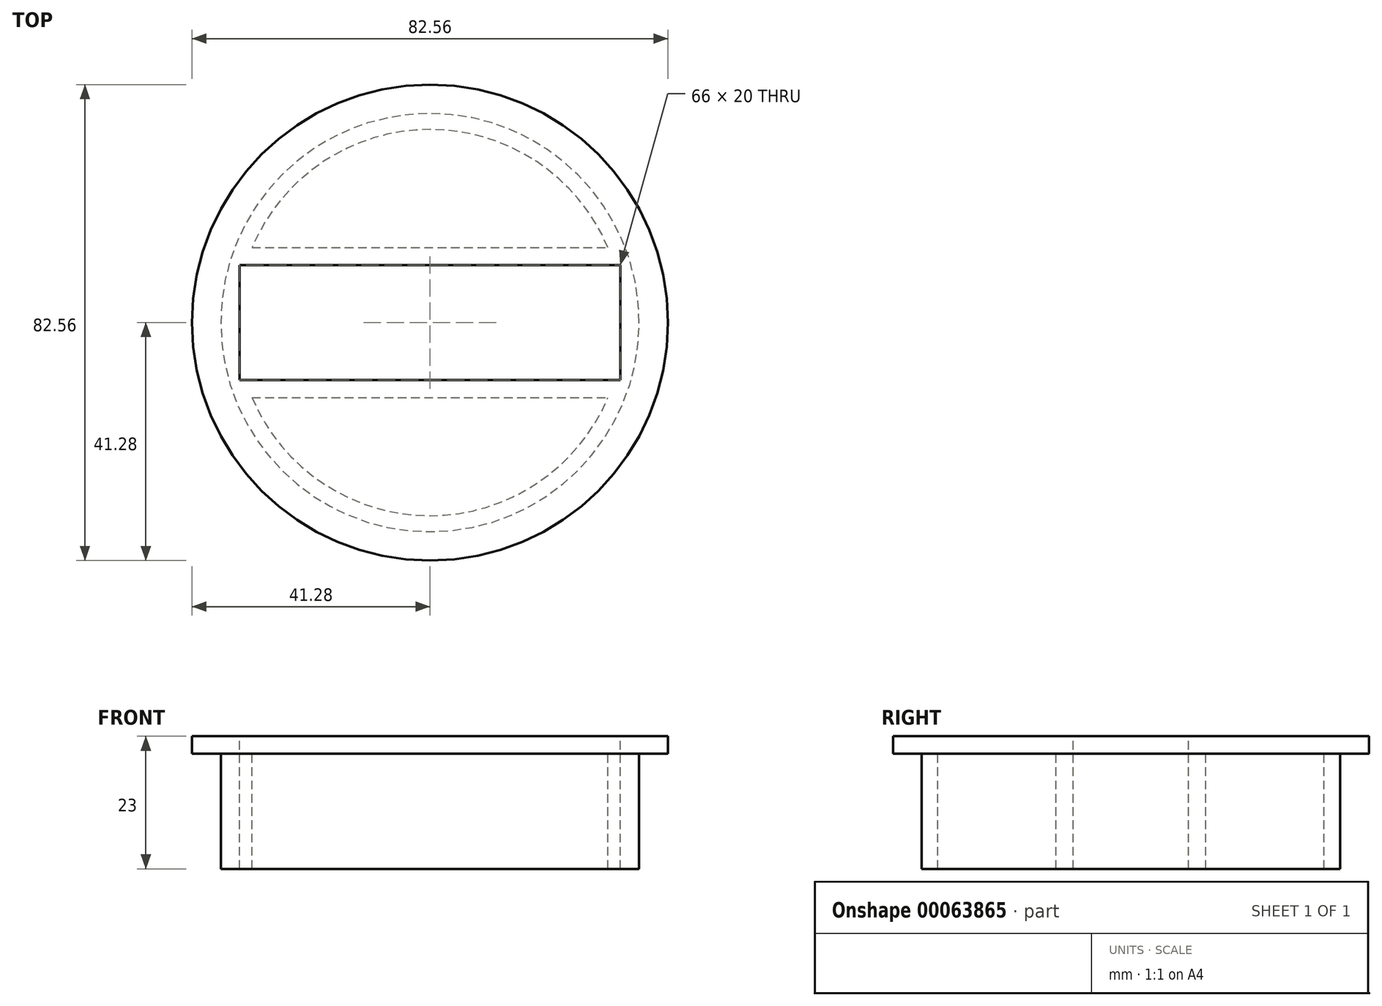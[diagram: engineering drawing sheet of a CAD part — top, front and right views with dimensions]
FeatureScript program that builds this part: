
annotation { "Feature Type Name" : "Feature", "Feature Type Description" : "" }
export const myFeature = defineFeature(function(context is Context, id is Id, definition is map)
    precondition{}
    {
        {
            var Q0;
            Q0=qCreatedBy(makeId("Top.planeOp"),FACE);
            var sketch = newSketch(context, id + "F0", { "sketchPlane" : qUnion([Q0])});
            skCircle(sketch, "E0", {"center": v(0, 0) * mm, "radius": 41.27 * mm});
            skSolve(sketch);
        }
        {
            var Q0;
            Q0 = qSketchRegion(id + "F0", true);
            extrude(context, id + "F1", {"entities" : qUnion([Q0]), "depth" : 3 * mm});
        }
        {
            var Q0;
            Q0=makeQuery(id+"F1.opExtrude","CAP_FACE",FACE,{"disambiguationData":[OSD([sQuery(id+"F0.wireOp",EDGE,"E0")])],"isStart":false});
            var sketch = newSketch(context, id + "F2", { "sketchPlane" : qUnion([Q0])});
            skLineSegment(sketch, "E1.rect.bottom", {"start": v(-33, -10) * mm, "end": v(33, -10) * mm});
            skLineSegment(sketch, "E1.rect.top", {"start": v(-33, 10) * mm, "end": v(33, 10) * mm});
            skLineSegment(sketch, "E1.rect.left", {"start": v(-33, -10) * mm, "end": v(-33, 10) * mm});
            skLineSegment(sketch, "E1.rect.right", {"start": v(33, -10) * mm, "end": v(33, 10) * mm});
            skPoint(sketch, "E1.rect.middle", {"position": v(0, 0) * mm});
            skSolve(sketch);
        }
        {
            var Q0;
            Q0=makeQuery(id+"F2.imprint","IMPRINT",FACE,{"disambiguationData":[TD([[makeQuery(id+"F2.imprint","IMPRINT",EDGE,{"derivedFrom":sQuery(id+"F2.wireOp",EDGE,"E1.rect.bottom")}),1.0]])]});
            extrude(context, id + "F3", {"entities" : qUnion([Q0]), "operationType" : NewBodyOperationType.REMOVE, "endBound" : BoundingType.THROUGH_ALL, "oppositeDirection" : true, "depth" : 25 * mm});
        }
        {
            var Q0;
            Q0=makeQuery(id+"F1.opExtrude","CAP_FACE",FACE,{"disambiguationData":[OSD([sQuery(id+"F0.wireOp",EDGE,"E0")])],"isStart":true});
            var sketch = newSketch(context, id + "F4", { "sketchPlane" : qUnion([Q0])});
            skCircle(sketch, "E2", {"center": v(0, 0) * mm, "radius": 36.5 * mm});
            skArc(sketch, "E3", {"start": v(30.87, 13) * mm, "mid": v(0, 33.5) * mm, "end": v(-30.87, 13) * mm});
            skLineSegment(sketch, "E4", {"start": v(33.5, 0) * mm, "end": v(36.5, 0) * mm});
            skLineSegment(sketch, "E5.0", {"start": v(-30.87, -13) * mm, "end": v(30.87, -13) * mm});
            skLineSegment(sketch, "E6.0", {"start": v(-30.87, 13) * mm, "end": v(30.87, 13) * mm});
            skCircle(sketch, "E7.0", {"center": v(0, 0) * mm, "radius": 36.27 * mm});
            skLineSegment(sketch, "E8.rect.bottom", {"start": v(-33, 10) * mm, "end": v(33, 10) * mm});
            skLineSegment(sketch, "E8.rect.top", {"start": v(-33, -10) * mm, "end": v(33, -10) * mm});
            skLineSegment(sketch, "E8.rect.left", {"start": v(-33, 10) * mm, "end": v(-33, -10) * mm});
            skLineSegment(sketch, "E8.rect.right", {"start": v(33, 10) * mm, "end": v(33, -10) * mm});
            skArc(sketch, "E9.trimOffspring", {"start": v(-30.87, -13) * mm, "mid": v(0, -33.5) * mm, "end": v(30.87, -13) * mm});
            skSolve(sketch);
        }
        {
            var Q0;
            Q0=makeQuery(id+"F4.imprint","IMPRINT",FACE,{"disambiguationData":[TD([[makeQuery(id+"F4.imprint","IMPRINT",EDGE,{"derivedFrom":sQuery(id+"F4.wireOp",EDGE,"E3")}),-1.0]])]});
            extrude(context, id + "F5", {"entities" : qUnion([Q0]), "operationType" : NewBodyOperationType.ADD, "depth" : 20 * mm});
        }
    });
